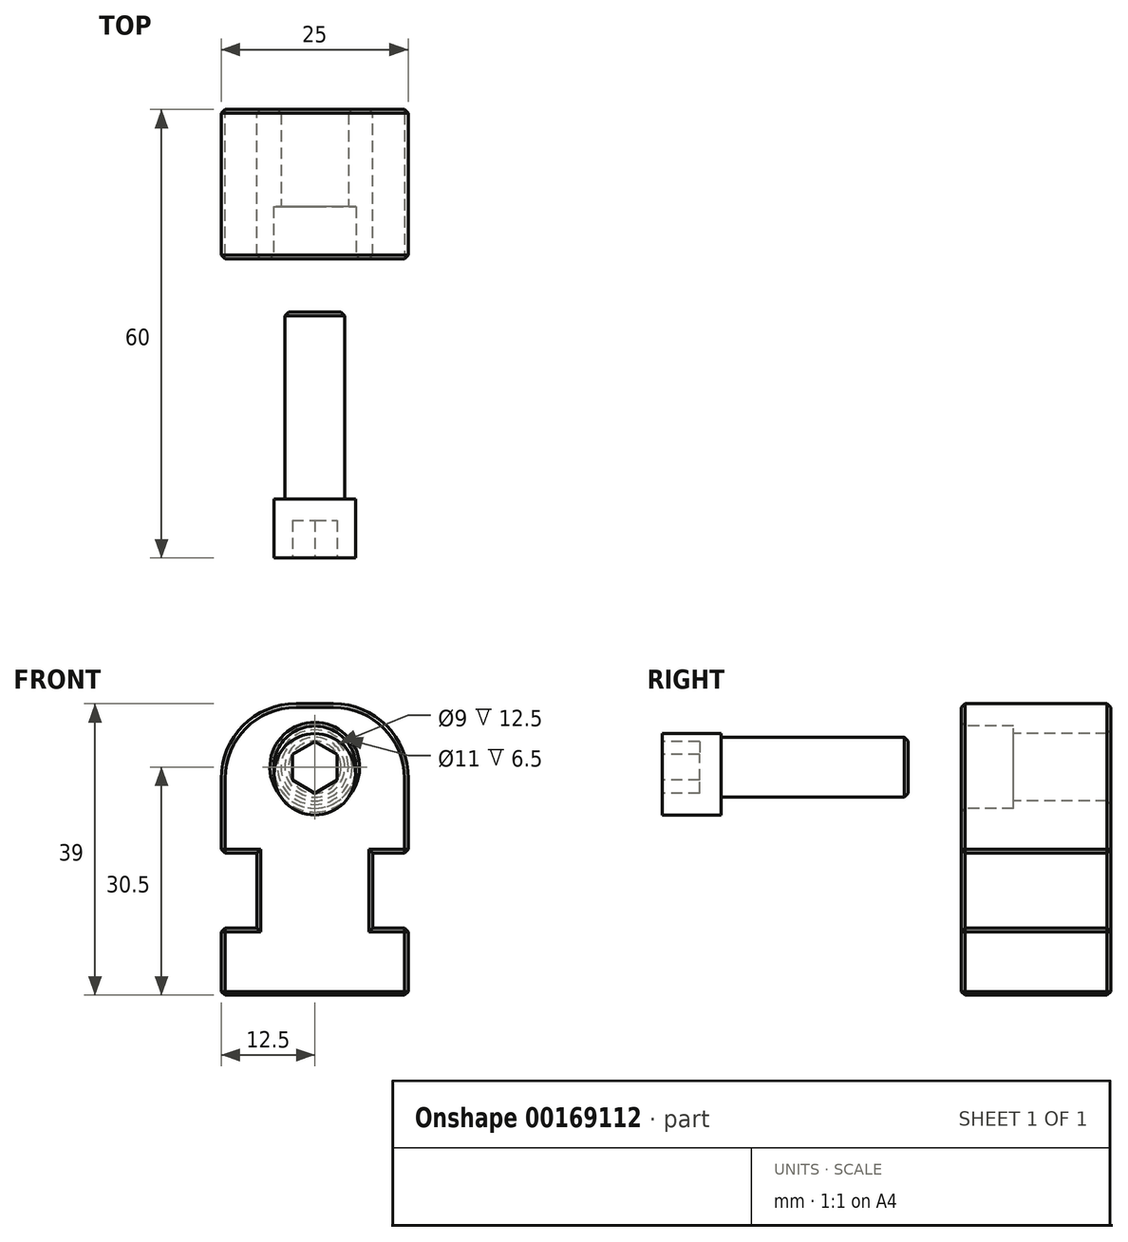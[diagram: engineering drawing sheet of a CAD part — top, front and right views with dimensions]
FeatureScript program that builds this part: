
annotation { "Feature Type Name" : "Feature", "Feature Type Description" : "" }
export const myFeature = defineFeature(function(context is Context, id is Id, definition is map)
    precondition{}
    {
        {
            var Q0;
            Q0=qCreatedBy(makeId("Front.planeOp"),FACE);
            var sketch = newSketch(context, id + "F0", { "sketchPlane" : qUnion([Q0])});
            skLineSegment(sketch, "E0", {"start": v(0, 0) * mm, "end": v(12.5, 0) * mm});
            skLineSegment(sketch, "E1", {"start": v(12.5, 0) * mm, "end": v(12.5, 9) * mm});
            skLineSegment(sketch, "E2", {"start": v(12.5, 9) * mm, "end": v(7.75, 9) * mm});
            skLineSegment(sketch, "E3", {"start": v(7.75, 9) * mm, "end": v(7.75, 19) * mm});
            skLineSegment(sketch, "E4", {"start": v(7.75, 19) * mm, "end": v(12.5, 19) * mm});
            skLineSegment(sketch, "E5", {"start": v(12.5, 19) * mm, "end": v(12.5, 39) * mm});
            skLineSegment(sketch, "E6", {"start": v(0, 0) * mm, "end": v(0, 38.2) * mm, "construction": true});
            skLineSegment(sketch, "E7", {"start": v(12.5, 39) * mm, "end": v(0, 39) * mm});
            skLineSegment(sketch, "E8.MirrorCS", {"start": v(0, 0) * mm, "end": v(-12.5, 0) * mm});
            skLineSegment(sketch, "E9.MirrorCS", {"start": v(-12.5, 0) * mm, "end": v(-12.5, 9) * mm});
            skLineSegment(sketch, "E10.MirrorCS", {"start": v(-12.5, 39) * mm, "end": v(0, 39) * mm});
            skLineSegment(sketch, "E11.MirrorCS", {"start": v(-12.5, 9) * mm, "end": v(-7.75, 9) * mm});
            skLineSegment(sketch, "E12.MirrorCS", {"start": v(-7.75, 19) * mm, "end": v(-12.5, 19) * mm});
            skLineSegment(sketch, "E13.MirrorCS", {"start": v(-7.75, 9) * mm, "end": v(-7.75, 19) * mm});
            skLineSegment(sketch, "E14.MirrorCS", {"start": v(-12.5, 19) * mm, "end": v(-12.5, 39) * mm});
            skSolve(sketch);
        }
        {
            var Q0;
            Q0=qSketchRegion(id+"F0",true);
            extrude(context, id + "F1", {"entities" : qUnion([Q0]), "depth" : 20 * mm});
        }
        {
            var Q0;
            Q0=makeQuery(id+"F1.opExtrude","SWEPT_EDGE",EDGE,{"disambiguationData":[OSD([sQuery(id+"F0.wireOp",EDGE,"E10.MirrorCS"),sQuery(id+"F0.wireOp",EDGE,"E14.MirrorCS")])]});
            var Q1;
            Q1=makeQuery(id+"F1.opExtrude","SWEPT_EDGE",EDGE,{"disambiguationData":[OSD([sQuery(id+"F0.wireOp",EDGE,"E5"),sQuery(id+"F0.wireOp",EDGE,"E7")])]});
            fillet(context, id + "F2", {"entities" : qUnion([Q0, Q1]), "radius" : 10 * mm, "tangentPropagation" : true, "allowEdgeOverflow" : false});
        }
        {
            var Q0;
            Q0=makeQuery(id+"F1.opExtrude","CAP_FACE",FACE,{"disambiguationData":[OSD([sQuery(id+"F0.wireOp",EDGE,"E0"),sQuery(id+"F0.wireOp",EDGE,"E1"),sQuery(id+"F0.wireOp",EDGE,"E2"),sQuery(id+"F0.wireOp",EDGE,"E3"),sQuery(id+"F0.wireOp",EDGE,"E4"),sQuery(id+"F0.wireOp",EDGE,"E5"),sQuery(id+"F0.wireOp",EDGE,"E7"),sQuery(id+"F0.wireOp",EDGE,"E8.MirrorCS"),sQuery(id+"F0.wireOp",EDGE,"E9.MirrorCS"),sQuery(id+"F0.wireOp",EDGE,"E10.MirrorCS"),sQuery(id+"F0.wireOp",EDGE,"E11.MirrorCS"),sQuery(id+"F0.wireOp",EDGE,"E12.MirrorCS"),sQuery(id+"F0.wireOp",EDGE,"E13.MirrorCS"),sQuery(id+"F0.wireOp",EDGE,"E14.MirrorCS")])],"isStart":false});
            var sketch = newSketch(context, id + "F3", { "sketchPlane" : qUnion([Q0])});
            skPoint(sketch, "E15", {"position": v(0, 30.5) * mm});
            skSolve(sketch);
        }
        {
            var Q0;
            Q0=sQuery(id+"F3.wireOp",VERTEX,"E15");
            var Q1;
            Q1=makeQuery(id+"F1.opExtrude","SWEPT_BODY",BODY,{"disambiguationData":[OSD([sQuery(id+"F0.wireOp",EDGE,"E0"),sQuery(id+"F0.wireOp",EDGE,"E1"),sQuery(id+"F0.wireOp",EDGE,"E2"),sQuery(id+"F0.wireOp",EDGE,"E3"),sQuery(id+"F0.wireOp",EDGE,"E4"),sQuery(id+"F0.wireOp",EDGE,"E5"),sQuery(id+"F0.wireOp",EDGE,"E7"),sQuery(id+"F0.wireOp",EDGE,"E8.MirrorCS"),sQuery(id+"F0.wireOp",EDGE,"E9.MirrorCS"),sQuery(id+"F0.wireOp",EDGE,"E10.MirrorCS"),sQuery(id+"F0.wireOp",EDGE,"E11.MirrorCS"),sQuery(id+"F0.wireOp",EDGE,"E12.MirrorCS"),sQuery(id+"F0.wireOp",EDGE,"E13.MirrorCS"),sQuery(id+"F0.wireOp",EDGE,"E14.MirrorCS")])]});
            hole(context, id + "F4", {"style" : HoleStyle.C_BORE, "endStyle" : HoleEndStyle.THROUGH, "holeDiameter" : 9 * mm, "cBoreDiameter" : 11 * mm, "cBoreDepth" : 7 * mm, "locations" : qUnion([Q0]), "scope" : qUnion([Q1]), "isTappedThrough" : true});
        }
        {
            var Q0;
            Q0=makeQuery(id+"F1.opExtrude","SWEPT_FACE",FACE,{"disambiguationData":[OSD([sQuery(id+"F0.wireOp",EDGE,"E7"),sQuery(id+"F0.wireOp",EDGE,"E10.MirrorCS")])]});
            var Q1;
            Q1=makeQuery(id+"F1.opExtrude","SWEPT_FACE",FACE,{"disambiguationData":[OSD([sQuery(id+"F0.wireOp",EDGE,"E5")])]});
            var Q2;
            Q2=makeQuery(id+"F1.opExtrude","SWEPT_FACE",FACE,{"disambiguationData":[OSD([sQuery(id+"F0.wireOp",EDGE,"E1")])]});
            var Q3;
            Q3=makeQuery(id+"F1.opExtrude","SWEPT_FACE",FACE,{"disambiguationData":[OSD([sQuery(id+"F0.wireOp",EDGE,"E0"),sQuery(id+"F0.wireOp",EDGE,"E8.MirrorCS")])]});
            var Q4;
            Q4=makeQuery(id+"F1.opExtrude","CAP_FACE",FACE,{"disambiguationData":[OSD([sQuery(id+"F0.wireOp",EDGE,"E0"),sQuery(id+"F0.wireOp",EDGE,"E1"),sQuery(id+"F0.wireOp",EDGE,"E2"),sQuery(id+"F0.wireOp",EDGE,"E3"),sQuery(id+"F0.wireOp",EDGE,"E4"),sQuery(id+"F0.wireOp",EDGE,"E5"),sQuery(id+"F0.wireOp",EDGE,"E7"),sQuery(id+"F0.wireOp",EDGE,"E8.MirrorCS"),sQuery(id+"F0.wireOp",EDGE,"E9.MirrorCS"),sQuery(id+"F0.wireOp",EDGE,"E10.MirrorCS"),sQuery(id+"F0.wireOp",EDGE,"E11.MirrorCS"),sQuery(id+"F0.wireOp",EDGE,"E12.MirrorCS"),sQuery(id+"F0.wireOp",EDGE,"E13.MirrorCS"),sQuery(id+"F0.wireOp",EDGE,"E14.MirrorCS")])],"isStart":false});
            var Q5;
            Q5=makeQuery(id+"F1.opExtrude","SWEPT_FACE",FACE,{"disambiguationData":[OSD([sQuery(id+"F0.wireOp",EDGE,"E9.MirrorCS")])]});
            var Q6;
            Q6=makeQuery(id+"F1.opExtrude","SWEPT_FACE",FACE,{"disambiguationData":[OSD([sQuery(id+"F0.wireOp",EDGE,"E14.MirrorCS")])]});
            var Q7;
            Q7=makeQuery(id+"F1.opExtrude","CAP_FACE",FACE,{"disambiguationData":[OSD([sQuery(id+"F0.wireOp",EDGE,"E0"),sQuery(id+"F0.wireOp",EDGE,"E1"),sQuery(id+"F0.wireOp",EDGE,"E2"),sQuery(id+"F0.wireOp",EDGE,"E3"),sQuery(id+"F0.wireOp",EDGE,"E4"),sQuery(id+"F0.wireOp",EDGE,"E5"),sQuery(id+"F0.wireOp",EDGE,"E7"),sQuery(id+"F0.wireOp",EDGE,"E8.MirrorCS"),sQuery(id+"F0.wireOp",EDGE,"E9.MirrorCS"),sQuery(id+"F0.wireOp",EDGE,"E10.MirrorCS"),sQuery(id+"F0.wireOp",EDGE,"E11.MirrorCS"),sQuery(id+"F0.wireOp",EDGE,"E12.MirrorCS"),sQuery(id+"F0.wireOp",EDGE,"E13.MirrorCS"),sQuery(id+"F0.wireOp",EDGE,"E14.MirrorCS")])],"isStart":true});
            chamfer(context, id + "F5", {"entities" : qUnion([Q0, Q1, Q2, Q3, Q4, Q5, Q6, Q7]), "width" : .5 * mm, "tangentPropagation" : true});
        }
        {
            var Q0;
            Q0=makeQuery(id+"F1.opExtrude","CAP_FACE",FACE,{"disambiguationData":[OSD([sQuery(id+"F0.wireOp",EDGE,"E0"),sQuery(id+"F0.wireOp",EDGE,"E1"),sQuery(id+"F0.wireOp",EDGE,"E2"),sQuery(id+"F0.wireOp",EDGE,"E3"),sQuery(id+"F0.wireOp",EDGE,"E4"),sQuery(id+"F0.wireOp",EDGE,"E5"),sQuery(id+"F0.wireOp",EDGE,"E7"),sQuery(id+"F0.wireOp",EDGE,"E8.MirrorCS"),sQuery(id+"F0.wireOp",EDGE,"E9.MirrorCS"),sQuery(id+"F0.wireOp",EDGE,"E10.MirrorCS"),sQuery(id+"F0.wireOp",EDGE,"E11.MirrorCS"),sQuery(id+"F0.wireOp",EDGE,"E12.MirrorCS"),sQuery(id+"F0.wireOp",EDGE,"E13.MirrorCS"),sQuery(id+"F0.wireOp",EDGE,"E14.MirrorCS")])],"isStart":false});
            cPlane(context, id + "F6", {"entities" : qUnion([Q0]), "cplaneType" : CPlaneType.OFFSET, "offset" : 40 * mm, "width" : 150 * mm, "height" : 150 * mm});
        }
        {
            var Q0;
            Q0=qCreatedBy(id+"F6.planeOp",FACE);
            var sketch = newSketch(context, id + "F7", { "sketchPlane" : qUnion([Q0])});
            skCircle(sketch, "E16", {"center": v(0, 30.5) * mm, "radius": 6.45 * mm});
            skSolve(sketch);
        }
        {
            var Q0;
            Q0=qSketchRegion(id+"F7",true);
            extrude(context, id + "F8", {"entities" : qUnion([Q0]), "oppositeDirection" : true, "depth" : 7.9 * mm});
        }
        {
            var Q0;
            Q0=makeQuery(id+"F8.opExtrude","CAP_FACE",FACE,{"disambiguationData":[OSD([sQuery(id+"F7.wireOp",EDGE,"E16")])],"isStart":true});
            var sketch = newSketch(context, id + "F9", { "sketchPlane" : qUnion([Q0])});
            skCircle(sketch, "E17.cCircle", {"center": v(0, 30.5) * mm, "radius": 3 * mm, "construction": true});
            skLineSegment(sketch, "E17.0", {"start": v(0, 33.96) * mm, "end": v(3, 32.23) * mm});
            skLineSegment(sketch, "E17.1", {"start": v(3, 32.23) * mm, "end": v(3, 28.77) * mm});
            skLineSegment(sketch, "E17.2", {"start": v(3, 28.77) * mm, "end": v(0, 27.04) * mm});
            skLineSegment(sketch, "E17.3", {"start": v(0, 27.04) * mm, "end": v(-3, 28.77) * mm});
            skLineSegment(sketch, "E17.4", {"start": v(-3, 28.77) * mm, "end": v(-3, 32.23) * mm});
            skLineSegment(sketch, "E17.5", {"start": v(-3, 32.23) * mm, "end": v(0, 33.96) * mm});
            skPoint(sketch, "E17.0.midPoint", {"position": v(1.5, 33.1) * mm});
            skSolve(sketch);
        }
        {
            var Q0;
            Q0=qSketchRegion(id+"F9",true);
            extrude(context, id + "F10", {"entities" : qUnion([Q0]), "operationType" : NewBodyOperationType.REMOVE, "oppositeDirection" : true, "depth" : 5 * mm});
        }
        {
            var Q0;
            Q0=makeQuery(id+"F8.opExtrude","CAP_FACE",FACE,{"disambiguationData":[OSD([sQuery(id+"F7.wireOp",EDGE,"E16")])],"isStart":false});
            var sketch = newSketch(context, id + "F11", { "sketchPlane" : qUnion([Q0])});
            skCircle(sketch, "E18", {"center": v(0, 30.5) * mm, "radius": 4 * mm});
            skSolve(sketch);
        }
        {
            var Q0;
            Q0=qSketchRegion(id+"F11",true);
            extrude(context, id + "F12", {"entities" : qUnion([Q0]), "operationType" : NewBodyOperationType.ADD, "depth" : 25 * mm});
        }
        {
            var Q0;
            Q0=makeQuery(id+"F12.opExtrude","CAP_EDGE",EDGE,{"disambiguationData":[OSD([sQuery(id+"F11.wireOp",EDGE,"E18")])],"isStart":false});
            chamfer(context, id + "F13", {"entities" : qUnion([Q0]), "width" : .5 * mm, "tangentPropagation" : true});
        }
        {
            var Q0;
            Q0=makeQuery(id+"F8.opExtrude","CAP_FACE",FACE,{"disambiguationData":[OSD([sQuery(id+"F7.wireOp",EDGE,"E16")])],"isStart":true});
            var sketch = newSketch(context, id + "F14", { "sketchPlane" : qUnion([Q0])});
            skCircle(sketch, "E19", {"center": v(0, 29.55) * mm, "radius": 5.45 * mm});
            skSolve(sketch);
        }
        {
            var Q0;
            Q0=makeQuery(id+"F14.imprint","IMPRINT",FACE,{"disambiguationData":[TD([[makeQuery(id+"F14.imprint","IMPRINT",EDGE,{"derivedFrom":sQuery(id+"F14.wireOp",EDGE,"E19")}),-1.0]])]});
            var Q1;
            Q1=makeQuery(id+"F8.opExtrude","CAP_FACE",FACE,{"disambiguationData":[OSD([sQuery(id+"F7.wireOp",EDGE,"E16")])],"isStart":false});
            extrude(context, id + "F15", {"entities" : qUnion([Q0]), "operationType" : NewBodyOperationType.REMOVE, "endBound" : BoundingType.UP_TO_SURFACE, "oppositeDirection" : true, "endBoundEntityFace" : qUnion([Q1]), "depth" : 25 * mm});
        }
    });
